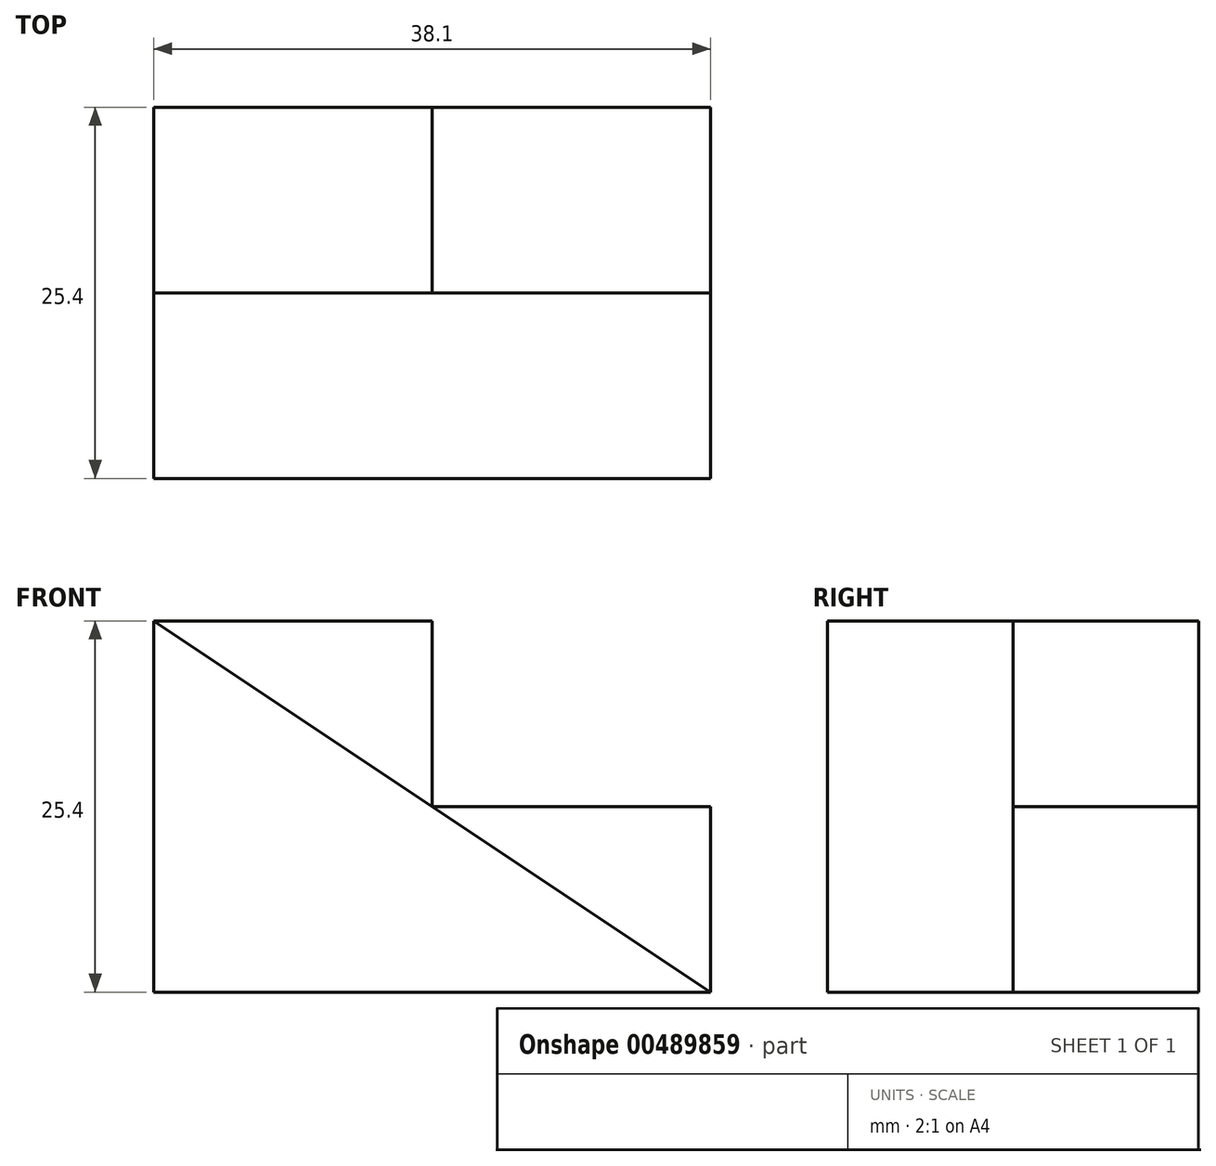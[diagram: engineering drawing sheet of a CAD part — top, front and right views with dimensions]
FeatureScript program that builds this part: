
annotation { "Feature Type Name" : "Feature", "Feature Type Description" : "" }
export const myFeature = defineFeature(function(context is Context, id is Id, definition is map)
    precondition{}
    {
        {
            var Q0;
            Q0=qCreatedBy(makeId("Front.planeOp"),FACE);
            var sketch = newSketch(context, id + "F0", { "sketchPlane" : qUnion([Q0])});
            skLineSegment(sketch, "E0.bottom", {"start": v(-45.73, 20.6) * mm, "end": v(-26.68, 20.6) * mm});
            skLineSegment(sketch, "E0.top", {"start": v(-45.73, 7.9) * mm, "end": v(-26.68, 7.9) * mm});
            skLineSegment(sketch, "E0.left", {"start": v(-45.73, 20.6) * mm, "end": v(-45.73, 7.9) * mm});
            skLineSegment(sketch, "E0.right", {"start": v(-26.68, 20.6) * mm, "end": v(-26.68, 7.9) * mm});
            skLineSegment(sketch, "E1.bottom", {"start": v(-45.73, 7.9) * mm, "end": v(-7.63, 7.9) * mm});
            skLineSegment(sketch, "E1.top", {"start": v(-45.73, -4.8) * mm, "end": v(-7.63, -4.8) * mm});
            skLineSegment(sketch, "E1.left", {"start": v(-45.73, 7.9) * mm, "end": v(-45.73, -4.8) * mm});
            skLineSegment(sketch, "E1.right", {"start": v(-7.63, 7.9) * mm, "end": v(-7.63, -4.8) * mm});
            skSolve(sketch);
        }
        {
            var Q0;
            Q0=makeQuery(id+"F0.imprint","IMPRINT",FACE,{"disambiguationData":[TD([[makeQuery(id+"F0.imprint","IMPRINT",EDGE,{"derivedFrom":sQuery(id+"F0.wireOp",EDGE,"E0.bottom")}),-1.0]])]});
            var Q1;
            Q1=makeQuery(id+"F0.imprint","IMPRINT",FACE,{"disambiguationData":[TD([[makeQuery(id+"F0.imprint","IMPRINT",EDGE,{"derivedFrom":sQuery(id+"F0.wireOp",EDGE,"E1.top")}),1.0]])]});
            extrude(context, id + "F1", {"entities" : qUnion([Q0, Q1]), "depth" : 12.7 * mm});
        }
        {
            var Q0;
            Q0=makeQuery(id+"F1.opExtrude","CAP_FACE",FACE,{"disambiguationData":[OSD([sQuery(id+"F0.wireOp",EDGE,"E0.bottom"),sQuery(id+"F0.wireOp",EDGE,"E0.left"),sQuery(id+"F0.wireOp",EDGE,"E0.right"),sQuery(id+"F0.wireOp",EDGE,"E1.bottom"),sQuery(id+"F0.wireOp",EDGE,"E1.top"),sQuery(id+"F0.wireOp",EDGE,"E1.left"),sQuery(id+"F0.wireOp",EDGE,"E1.right")])],"isStart":false});
            var sketch = newSketch(context, id + "F2", { "sketchPlane" : qUnion([Q0])});
            skLineSegment(sketch, "E2", {"start": v(-45.73, 20.6) * mm, "end": v(-7.63, -4.8) * mm});
            skLineSegment(sketch, "E3", {"start": v(-7.63, -4.8) * mm, "end": v(-45.73, -4.8) * mm});
            skLineSegment(sketch, "E4", {"start": v(-45.73, -4.8) * mm, "end": v(-45.73, 18.42) * mm});
            skSolve(sketch);
        }
        {
            var Q0;
            {var subQ1=sQuery(id+"F2.wireOp",EDGE,"E3");Q0=makeQuery(id+"F2.imprint","IMPRINT",FACE,{"disambiguationData":[TD([[makeQuery(id+"F2.imprint","IMPRINT",EDGE,{"derivedFrom":subQ1}),1.0]])]});}
            extrude(context, id + "F3", {"entities" : qUnion([Q0]), "operationType" : NewBodyOperationType.ADD, "depth" : 12.7 * mm});
        }
    });
